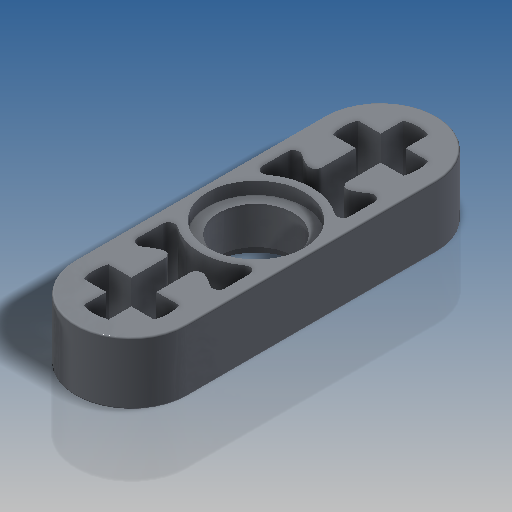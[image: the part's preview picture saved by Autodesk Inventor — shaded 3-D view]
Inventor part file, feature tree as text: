
AUTODESK INVENTOR PART (.ipt)
format: ipt  version: 2018.3 (Build 223284000, 284)  size: 270,336 bytes
history: native  units: mm
features: extrude x2, sketch x2, mirror x1, fillet x1
ambient origin geometry x8: Origin, YZ Plane, XZ Plane, XY Plane, X Axis, Y Axis, Z Axis, Center Point
bodies: Solid1 (feature_tree)
feature tree (6):
  extrude  "Extrusion1"  Depth=6.4mm
  extrude  "Extrusion7"  Depth=7.2mm
  mirror  "Mirror1"
  fillet  "Fillet1"  Radius=8.0mm
  sketch  "Sketch1"  dims[d8=4.8mm d9=6.4mm]
  sketch  "Sketch6"  dims[d14=4.0mm d15=0.0mm d32=7.2mm d34=8.0mm d36=0.8mm d41=0.8mm d42=0.0mm d45=0.1mm d46=0.4mm d52=1.6mm d53=6.2mm]
